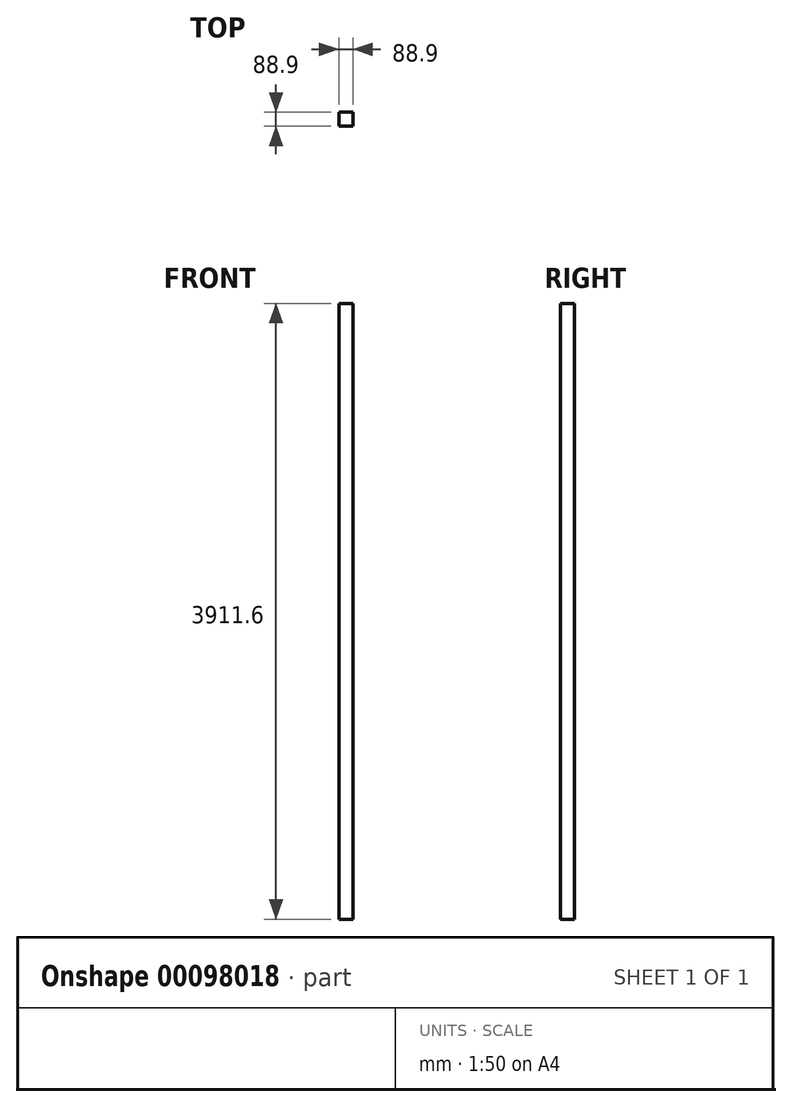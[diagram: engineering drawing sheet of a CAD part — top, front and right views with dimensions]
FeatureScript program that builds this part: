
annotation { "Feature Type Name" : "Feature", "Feature Type Description" : "" }
export const myFeature = defineFeature(function(context is Context, id is Id, definition is map)
    precondition{}
    {
        {
            var Q0;
            Q0=qCreatedBy(makeId("Front.planeOp"),FACE);
            var sketch = newSketch(context, id + "F0", { "sketchPlane" : qUnion([Q0])});
            skLineSegment(sketch, "E0.bottom", {"start": v(44.45, 1955.8) * mm, "end": v(-44.45, 1955.8) * mm});
            skLineSegment(sketch, "E0.top", {"start": v(44.45, -1955.8) * mm, "end": v(-44.45, -1955.8) * mm});
            skLineSegment(sketch, "E0.left", {"start": v(44.45, 1955.8) * mm, "end": v(44.45, -1955.8) * mm});
            skLineSegment(sketch, "E0.right", {"start": v(-44.45, 1955.8) * mm, "end": v(-44.45, -1955.8) * mm});
            skPoint(sketch, "E0.middle", {"position": v(0, 0) * mm});
            skSolve(sketch);
        }
        {
            var Q0;
            Q0=makeQuery(id+"F0.imprint","IMPRINT",FACE,{"disambiguationData":[TD([[makeQuery(id+"F0.imprint","IMPRINT",EDGE,{"derivedFrom":sQuery(id+"F0.wireOp",EDGE,"E0.bottom")}),1.0]])]});
            extrude(context, id + "F1", {"entities" : qUnion([Q0]), "depth" : 88.9 * mm});
        }
    });
